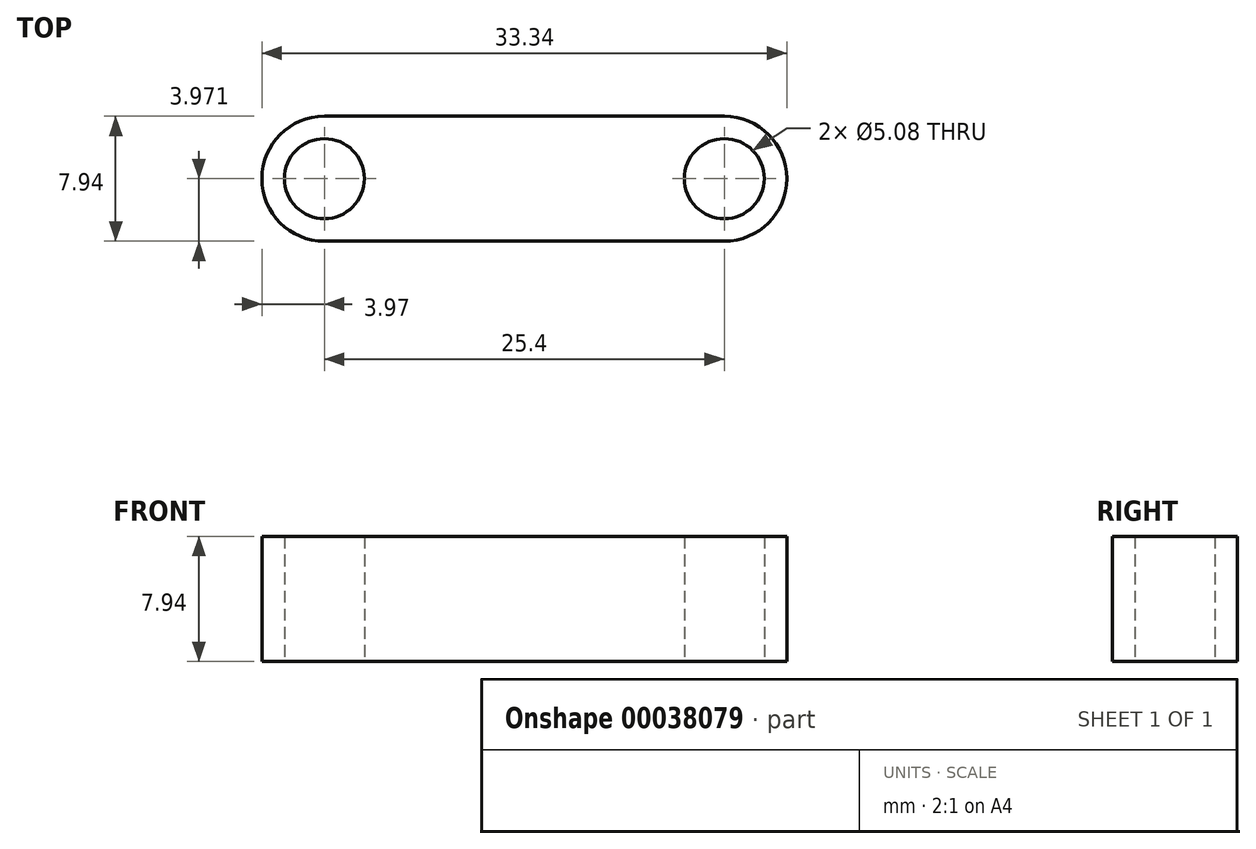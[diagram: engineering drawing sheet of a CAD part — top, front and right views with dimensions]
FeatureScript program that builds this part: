
annotation { "Feature Type Name" : "Feature", "Feature Type Description" : "" }
export const myFeature = defineFeature(function(context is Context, id is Id, definition is map)
    precondition{}
    {
        {
            var Q0;
            Q0=qCreatedBy(makeId("Top.planeOp"),FACE);
            var sketch = newSketch(context, id + "F0", { "sketchPlane" : qUnion([Q0])});
            skLineSegment(sketch, "E0.bottom", {"start": v(0, 0) * mm, "end": v(25.4, 0) * mm});
            skLineSegment(sketch, "E0.top", {"start": v(0, -7.94) * mm, "end": v(25.4, -7.94) * mm});
            skLineSegment(sketch, "E0.left", {"start": v(0, 0) * mm, "end": v(0, -7.94) * mm, "construction": true});
            skLineSegment(sketch, "E0.right", {"start": v(25.4, 0) * mm, "end": v(25.4, -7.94) * mm, "construction": true});
            skArc(sketch, "E1", {"start": v(0, 0) * mm, "mid": v(-3.97, -3.97) * mm, "end": v(0, -7.94) * mm});
            skArc(sketch, "E2", {"start": v(25.4, -7.94) * mm, "mid": v(29.37, -3.97) * mm, "end": v(25.4, 0) * mm});
            skCircle(sketch, "E3", {"center": v(0, -3.97) * mm, "radius": 2.54 * mm});
            skCircle(sketch, "E4", {"center": v(25.4, -3.97) * mm, "radius": 2.54 * mm});
            skSolve(sketch);
        }
        {
            var Q0;
            Q0=qSketchRegion(id+"F0",true);
            extrude(context, id + "F1", {"entities" : qUnion([Q0]), "depth" : 7.94 * mm});
        }
    });
